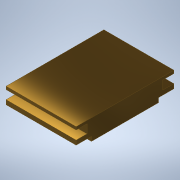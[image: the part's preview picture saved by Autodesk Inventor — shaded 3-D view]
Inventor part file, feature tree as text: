
AUTODESK INVENTOR PART (.ipt)
format: ipt  version: 2022 (Build 260153000, 153)  size: 176,640 bytes
history: native  units: in
note: dims shown in document units (in); Inventor stores cm internally (conversion verified against a paired STEP export)
features: extrude x5, sketch x5
ambient origin geometry x8: Origin, YZ Plane, XZ Plane, XY Plane, X Axis, Y Axis, Z Axis, Center Point
bodies: Solid1 (feature_tree)
feature tree (10):
  extrude  "Extrusion1"  Depth=1.8898in
  extrude  "Extrusion4"  Depth=0.0787in
  extrude  "Extrusion5"  Depth=0.1181in
  extrude  "Extrusion6"  Depth=0.1181in
  extrude  "Extrusion7"  Depth=0.1181in
  sketch  "Sketch1"  dims[d0=2.0472in d1=1.8898in]
  sketch  "Sketch4"  dims[d2=0.5512in d3=0.0in d14=0.0787in]
  sketch  "Sketch6"  dims[d17=0.2953in d18=0.0in d21=0.1181in]
  sketch  "Sketch7"  dims[d22=0.2953in d23=0.0in d24=0.1969in d25=0.4331in d26=0.4331in d27=0.7874in d29=0.8661in d30=0.7874in d32=0.8661in d35=0.0787in d36=0.0in d37=0.1181in d38=0.1181in d39=0.0in d40=0.0in]
  sketch  "Sketch5"  dims[d15=0.1181in d16=0.1181in]
